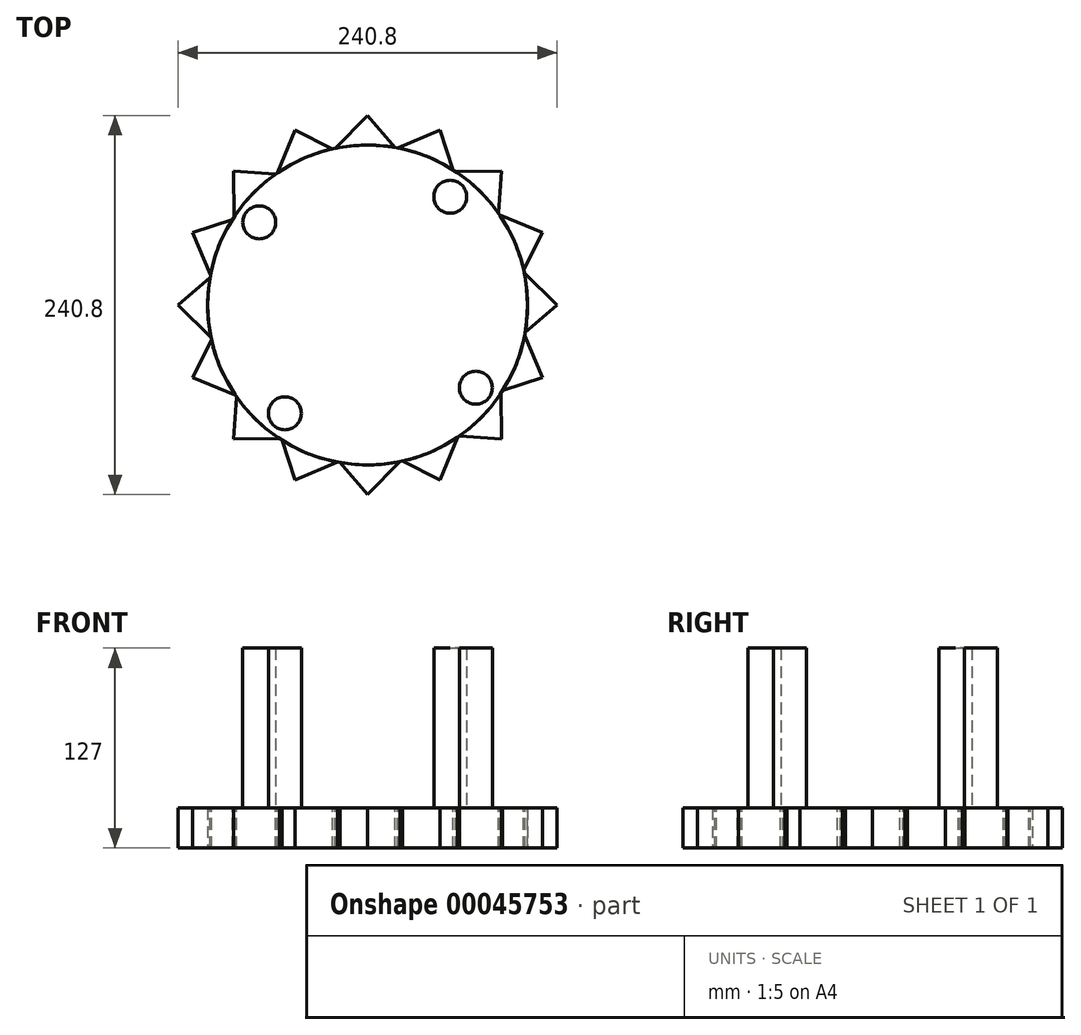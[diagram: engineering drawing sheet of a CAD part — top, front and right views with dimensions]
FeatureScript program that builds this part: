
annotation { "Feature Type Name" : "Feature", "Feature Type Description" : "" }
export const myFeature = defineFeature(function(context is Context, id is Id, definition is map)
    precondition{}
    {
        {
            var Q0;
            Q0=qCreatedBy(makeId("Top.planeOp"),FACE);
            var sketch = newSketch(context, id + "F0", { "sketchPlane" : qUnion([Q0])});
            skCircle(sketch, "E0", {"center": v(0, 0) * mm, "radius": 101.6 * mm});
            skSolve(sketch);
        }
        {
            var Q0;
            Q0=makeQuery(id+"F0.imprint","IMPRINT",FACE,{"disambiguationData":[TD([[makeQuery(id+"F0.imprint","IMPRINT",EDGE,{"derivedFrom":sQuery(id+"F0.wireOp",EDGE,"E0")}),1.0]])]});
            extrude(context, id + "F1", {"entities" : qUnion([Q0]), "endBound" : BoundingType.SYMMETRIC, "depth" : 25.4 * mm});
        }
        {
            var Q0;
            Q0=makeQuery(id+"F1.opExtrude","CAP_FACE",FACE,{"disambiguationData":[OSD([sQuery(id+"F0.wireOp",EDGE,"E0")])],"isStart":false});
            var sketch = newSketch(context, id + "F2", { "sketchPlane" : qUnion([Q0])});
            skCircle(sketch, "E1", {"center": v(-68.75, 52.52) * mm, "radius": 10.47 * mm});
            skSolve(sketch);
        }
        {
            var Q0;
            Q0 = qSketchRegion(id + "F2", true);
            extrude(context, id + "F3", {"entities" : qUnion([Q0]), "depth" : 101.6 * mm});
        }
        {
            var Q0;
            Q0=makeQuery(id+"F3.opExtrude","SWEPT_BODY",BODY,{"disambiguationData":[OSD([sQuery(id+"F2.wireOp",EDGE,"E1")])]});
            var Q1;
            Q1=makeQuery(id+"F1.opExtrude","CAP_EDGE",EDGE,{"disambiguationData":[OSD([sQuery(id+"F0.wireOp",EDGE,"E0")])],"isStart":false});
            circularPattern(context, id + "F4", {"entities" : qUnion([Q0]), "axis" : qUnion([Q1]), "angle" : 360 * degree, "instanceCount" : 4, "equalSpace" : true});
        }
        {
            var Q0;
            Q0=makeQuery(id+"F1.opExtrude","CAP_FACE",FACE,{"disambiguationData":[OSD([sQuery(id+"F0.wireOp",EDGE,"E0")])],"isStart":false});
            var sketch = newSketch(context, id + "F5", { "sketchPlane" : qUnion([Q0])});
            skLineSegment(sketch, "E2", {"start": v(-20.56, 99.5) * mm, "end": v(0, 120.4) * mm});
            skLineSegment(sketch, "E3", {"start": v(0, 120.4) * mm, "end": v(17.38, 100.1) * mm});
            skSolve(sketch);
        }
        {
            var Q0;
            {var subQ2=sQuery(id+"F5.wireOp",EDGE,"E2");Q0=makeQuery(id+"F5.imprint","IMPRINT",FACE,{"disambiguationData":[TD([[makeQuery(id+"F5.imprint","IMPRINT",EDGE,{"derivedFrom":subQ2}),-1.0]])]});}
            var Q1;
            Q1=makeQuery(id+"F1.opExtrude","CAP_FACE",FACE,{"disambiguationData":[OSD([sQuery(id+"F0.wireOp",EDGE,"E0")])],"isStart":true});
            extrude(context, id + "F6", {"entities" : qUnion([Q0]), "endBound" : BoundingType.UP_TO_SURFACE, "oppositeDirection" : true, "endBoundEntityFace" : qUnion([Q1]), "depth" : 25.4 * mm});
        }
        {
            var Q0;
            Q0=makeQuery(id+"F6.opExtrude","SWEPT_BODY",BODY,{"disambiguationData":[OSD([sQuery(id+"F0.wireOp",EDGE,"E0"),sQuery(id+"F5.wireOp",EDGE,"E2"),sQuery(id+"F5.wireOp",EDGE,"E3")])]});
            var Q1;
            Q1=makeQuery(id+"F1.opExtrude","CAP_EDGE",EDGE,{"disambiguationData":[OSD([sQuery(id+"F0.wireOp",EDGE,"E0")])],"isStart":false});
            circularPattern(context, id + "F7", {"entities" : qUnion([Q0]), "axis" : qUnion([Q1]), "angle" : 360 * degree, "instanceCount" : 16, "equalSpace" : true});
        }
    });
